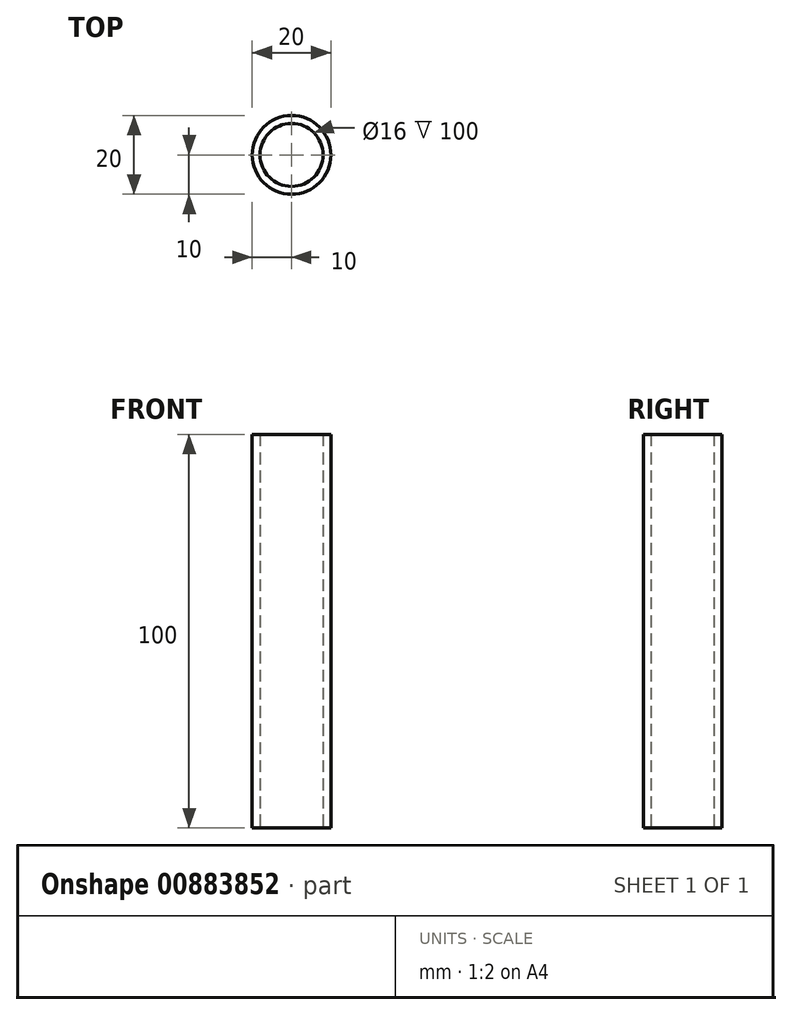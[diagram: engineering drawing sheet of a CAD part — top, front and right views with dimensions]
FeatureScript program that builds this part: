
annotation { "Feature Type Name" : "Feature", "Feature Type Description" : "" }
export const myFeature = defineFeature(function(context is Context, id is Id, definition is map)
    precondition{}
    {
        {
            var Q0;
            Q0=qCreatedBy(makeId("Front.planeOp"),FACE);
            var sketch = newSketch(context, id + "F0", { "sketchPlane" : qUnion([Q0])});
            skLineSegment(sketch, "E0", {"start": v(0, 0) * mm, "end": v(0, 107.75) * mm, "construction": true});
            skLineSegment(sketch, "E1", {"start": v(10, 0) * mm, "end": v(10, 100) * mm});
            skLineSegment(sketch, "E2", {"start": v(8, 100) * mm, "end": v(10, 100) * mm});
            skLineSegment(sketch, "E3", {"start": v(8, 100) * mm, "end": v(8, 0) * mm});
            skLineSegment(sketch, "E4", {"start": v(10, 0) * mm, "end": v(8, 0) * mm});
            skSolve(sketch);
        }
        {
            var Q0;
            Q0=makeQuery(id+"F0.imprint","IMPRINT",FACE,{"disambiguationData":[TD([[makeQuery(id+"F0.imprint","IMPRINT",EDGE,{"derivedFrom":sQuery(id+"F0.wireOp",EDGE,"E1")}),1.0]])]});
            var Q1;
            Q1=sQuery(id+"F0.wireOp",EDGE,"E0");
            revolve(context, id + "F1", {"surfaceOperationType" : NewSurfaceOperationType.NEW, "entities" : qUnion([Q0]), "axis" : qUnion([Q1]), "revolveType" : RevolveType.FULL});
        }
    });
